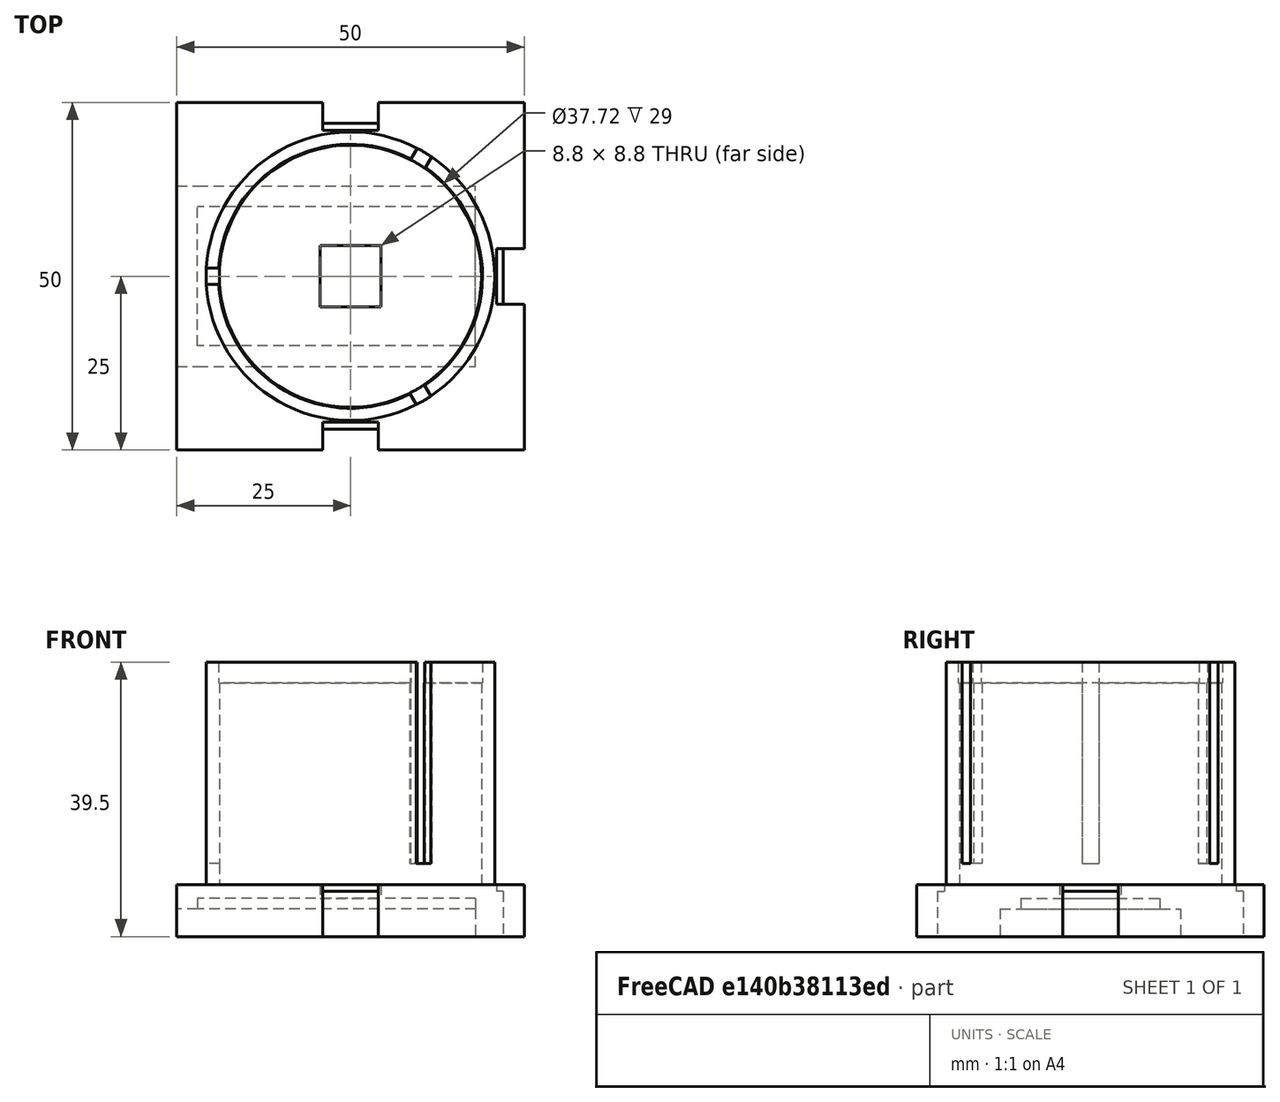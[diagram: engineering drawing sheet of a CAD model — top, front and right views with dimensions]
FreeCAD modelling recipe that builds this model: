
FCSTD DOCUMENT  (FreeCAD 0.16R6712 (Git))
Label: mount
License: All rights reserved
LicenseURL: http://en.wikipedia.org/wiki/All_rights_reserved
objects: Part::FeaturePython×17, Part::Box×13, Part::Cylinder×3
note: 33 computed .brp shape members not serialized (recipe doc carries the construction recipe); baked Part::Feature solids carry a one-line shape summary decoded from their .brp

FEATURE [Part::Box] Box  label="Base"
  Height = 7.5
  Length = 50
  Placement = pos=(-25,-25,0) rot=(0,0,1;0rad)
  Width = 50
FEATURE [Part::Box] Box001  label="立方体001"
  Height = 7
  Length = 40
  Placement = pos=(-18,-13,2) rot=(0,0,1;0rad)
  Width = 26
FEATURE [Part::FeaturePython] Cutout  # WARN: FeaturePython — macro-defined, semantics opaque (R4)
  Base = -> Box
  Mode = 3
  Tool = -> Box001
FEATURE [Part::Box] Box002  label="立方体"
  Height = 3
  Length = 8.8
  Placement = pos=(-4.4,-4.4,0) rot=(0,0,1;0rad)
  Width = 8.8
FEATURE [Part::FeaturePython] Cutout001  # WARN: FeaturePython — macro-defined, semantics opaque (R4)
  Base = -> Cutout
  Mode = 3
  Tool = -> Box002
FEATURE [Part::Box] Box003  label="立方体002"
  Height = 1.5
  Length = 41
  Placement = pos=(-18,10,2) rot=(0,0,1;0rad)
  Width = 4
FEATURE [Part::Box] Box004  label="立方体003"
  Height = 1.5
  Length = 41
  Placement = pos=(-18,-14,2) rot=(0,0,1;0rad)
  Width = 4
FEATURE [Part::FeaturePython] Connect  # WARN: FeaturePython — macro-defined, semantics opaque (R4)
  Base = -> Box003
  Mode = 1
  Tool = -> Cutout001
FEATURE [Part::FeaturePython] Connect001  # WARN: FeaturePython — macro-defined, semantics opaque (R4)
  Base = -> Box004
  Mode = 1
  Tool = -> Connect
FEATURE [Part::Box] Box005  label="立方体004"
  Height = 5.5
  Length = 3
  Placement = pos=(22,-13,3.5) rot=(0,0,1;0rad)
  Width = 26
FEATURE [Part::FeaturePython] Cutout002  # WARN: FeaturePython — macro-defined, semantics opaque (R4)
  Base = -> Connect001
  Mode = 3
  Tool = -> Box005
FEATURE [Part::Box] Box006  label="clip"
  Height = 9.5
  Length = 8
  Placement = pos=(-4,-32,-2) rot=(0,0,1;0rad)
  Width = 3
FEATURE [Part::Box] Box007  label="立方体005"
  Height = 3
  Length = 8
  Placement = pos=(-4,-30,-2) rot=(0,0,1;0rad)
  Width = 2
FEATURE [Part::FeaturePython] Connect002  label="Clip001"  # WARN: FeaturePython — macro-defined, semantics opaque (R4)
  Base = -> Box006
  Mode = 1
  Placement = pos=(0,7,0) rot=(0,0,1;0rad)
  Tool = -> Box007
FEATURE [Part::FeaturePython] Connect003  label="Clip002"  # WARN: FeaturePython — macro-defined, semantics opaque (R4)
  Base = -> Box006
  Mode = 1
  Placement = pos=(0,-7,0) rot=(0,0,1;3.14159rad)
  Tool = -> Box007
FEATURE [Part::Box] Box008  label="clip001"
  Height = 9.5
  Length = 8
  Placement = pos=(-4,-32,-2) rot=(0,0,1;0rad)
  Width = 3
FEATURE [Part::Box] Box009  label="立方体006"
  Height = 3
  Length = 8
  Placement = pos=(-4,-30,-2) rot=(0,0,1;0rad)
  Width = 2
FEATURE [Part::FeaturePython] Connect004  label="Clip003"  # WARN: FeaturePython — macro-defined, semantics opaque (R4)
  Base = -> Box008
  Mode = 1
  Placement = pos=(7,0,0) rot=(0,0,-1;1.5708rad)
  Tool = -> Box009
FEATURE [Part::FeaturePython] Cutout003  # WARN: FeaturePython — macro-defined, semantics opaque (R4)
  Base = -> Cutout002
  Mode = 3
  Tool = -> Connect002
FEATURE [Part::FeaturePython] Cutout004  # WARN: FeaturePython — macro-defined, semantics opaque (R4)
  Base = -> Cutout003
  Mode = 3
  Tool = -> Connect003
FEATURE [Part::FeaturePython] Cutout005  label="Holder"  # WARN: FeaturePython — macro-defined, semantics opaque (R4)
  Base = -> Cutout004
  Mode = 3
  Tool = -> Connect004
FEATURE [Part::Cylinder] Cylinder  label="圆柱体"
  Angle = 360
  Height = 32
  Placement = pos=(0,0,-37) rot=(0,0,1;0rad)
  Radius = 20.76
FEATURE [Part::Cylinder] Cylinder001  label="圆柱体001"
  Angle = 360
  Height = 32
  Placement = pos=(0,0,-34) rot=(0,0,1;0rad)
  Radius = 18.86
FEATURE [Part::FeaturePython] Cutout006  # WARN: FeaturePython — macro-defined, semantics opaque (R4)
  Base = -> Cylinder
  Mode = 3
  Tool = -> Cylinder001
FEATURE [Part::Cylinder] Cylinder002  label="圆柱体002"
  Angle = 360
  Height = 3
  Placement = pos=(0,0,-37) rot=(0,0,1;0rad)
  Radius = 19
FEATURE [Part::FeaturePython] Cutout007  label="Tube"  # WARN: FeaturePython — macro-defined, semantics opaque (R4)
  Base = -> Cutout006
  Mode = 3
  Placement = pos=(0,0,5) rot=(0,0,1;0rad)
  Tool = -> Cylinder002
FEATURE [Part::Box] Box010  label="立方体007"
  Height = 29
  Length = 22
  Placement = pos=(0,-1.2,-32) rot=(0,0,1;0rad)
  Width = 2.4
FEATURE [Part::Box] Box011  label="立方体008"
  Height = 29
  Length = 22
  Placement = pos=(1,0,-32) rot=(0,0,1;2.0944rad)
  Width = 2.4
FEATURE [Part::Box] Box012  label="立方体009"
  Height = 29
  Length = 22
  Placement = pos=(-1,1,-32) rot=(0,0,-1;2.0944rad)
  Width = 2.4
FEATURE [Part::FeaturePython] Cutout008  # WARN: FeaturePython — macro-defined, semantics opaque (R4)
  Base = -> Cutout007
  Mode = 3
  Tool = -> Box010
FEATURE [Part::FeaturePython] Cutout009  # WARN: FeaturePython — macro-defined, semantics opaque (R4)
  Base = -> Cutout008
  Mode = 3
  Tool = -> Box011
FEATURE [Part::FeaturePython] Cutout010  label="TubeWithCut"  # WARN: FeaturePython — macro-defined, semantics opaque (R4)
  Base = -> Cutout009
  Mode = 3
  Tool = -> Box012
FEATURE [Part::FeaturePython] Connect005  # WARN: FeaturePython — macro-defined, semantics opaque (R4)
  Base = -> Cutout005
  Mode = 1
  Placement = pos=(0,0,7) rot=(0,1,0;3.14159rad)
  Tool = -> Cutout010
